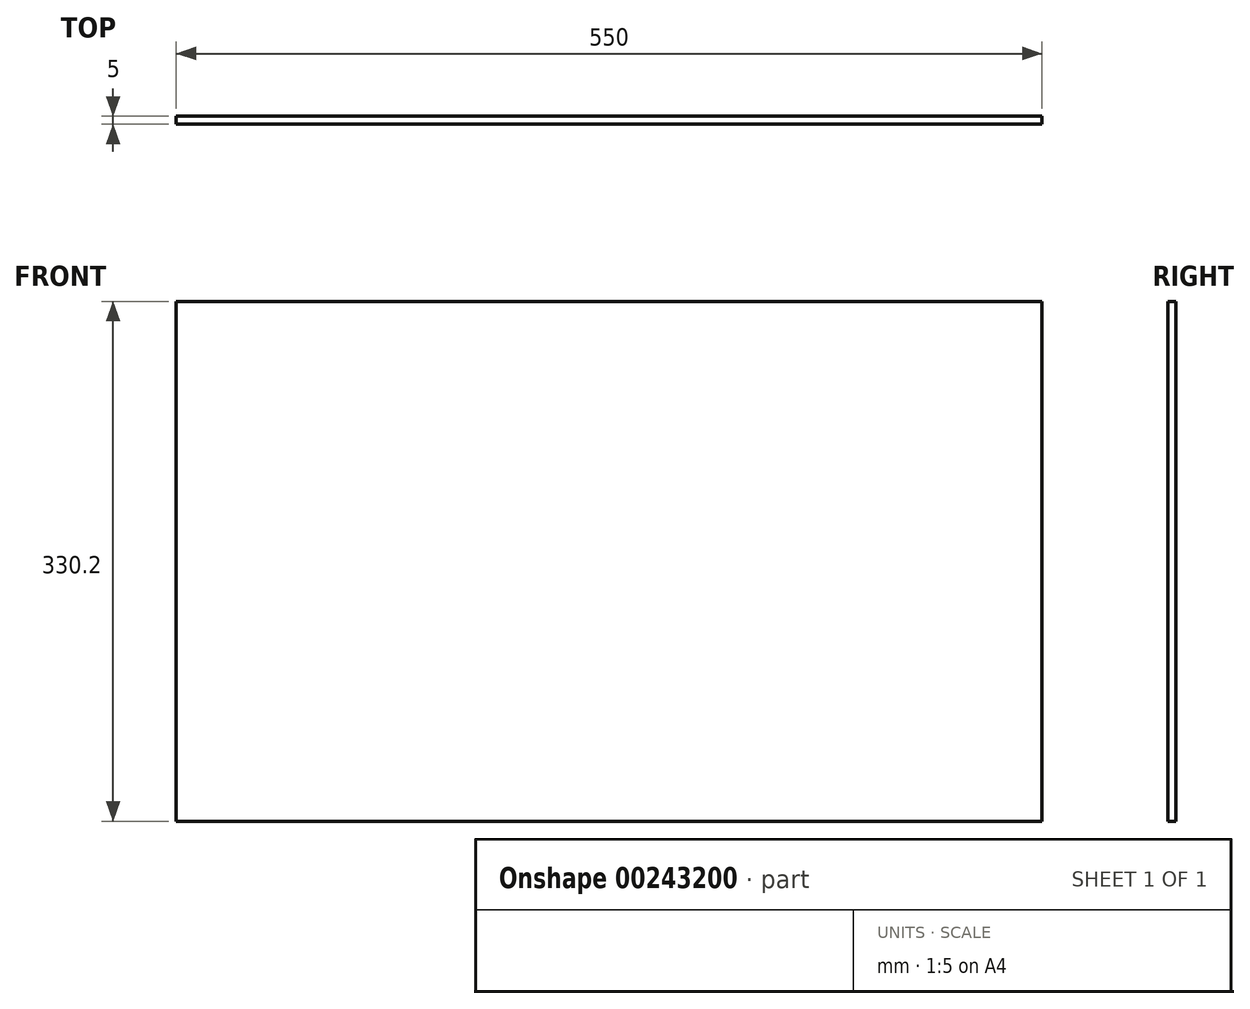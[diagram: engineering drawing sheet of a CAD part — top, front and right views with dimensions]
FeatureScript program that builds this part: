
annotation { "Feature Type Name" : "Feature", "Feature Type Description" : "" }
export const myFeature = defineFeature(function(context is Context, id is Id, definition is map)
    precondition{}
    {
        {
            var Q0;
            Q0=qCreatedBy(makeId("Front.planeOp"),FACE);
            var sketch = newSketch(context, id + "F0", { "sketchPlane" : qUnion([Q0])});
            skLineSegment(sketch, "E0.bottom", {"start": v(-191.75, 43.45) * mm, "end": v(113.25, 43.45) * mm});
            skLineSegment(sketch, "E0.top", {"start": v(-191.75, -73.55) * mm, "end": v(113.25, -73.55) * mm});
            skLineSegment(sketch, "E0.left", {"start": v(-191.75, 43.45) * mm, "end": v(-191.75, -73.55) * mm});
            skLineSegment(sketch, "E0.right", {"start": v(113.25, 43.45) * mm, "end": v(113.25, -73.55) * mm});
            skLineSegment(sketch, "E1.bottom", {"start": v(-203.2, 168.67) * mm, "end": v(0, 168.67) * mm});
            skLineSegment(sketch, "E1.top", {"start": v(-203.2, 98.67) * mm, "end": v(0, 98.67) * mm});
            skLineSegment(sketch, "E1.left", {"start": v(-203.2, 168.67) * mm, "end": v(-203.2, 98.67) * mm});
            skLineSegment(sketch, "E1.right", {"start": v(0, 168.67) * mm, "end": v(0, 98.67) * mm});
            skLineSegment(sketch, "E2.bottom", {"start": v(-191.58, -90.92) * mm, "end": v(11.62, -90.92) * mm});
            skLineSegment(sketch, "E2.top", {"start": v(-191.58, -160.92) * mm, "end": v(11.62, -160.92) * mm});
            skLineSegment(sketch, "E2.left", {"start": v(-191.58, -90.92) * mm, "end": v(-191.58, -160.92) * mm});
            skLineSegment(sketch, "E2.right", {"start": v(11.62, -90.92) * mm, "end": v(11.62, -160.92) * mm});
            skLineSegment(sketch, "E3.bottom", {"start": v(-312.35, 526.53) * mm, "end": v(237.65, 526.53) * mm});
            skLineSegment(sketch, "E3.top", {"start": v(-312.35, 196.33) * mm, "end": v(237.65, 196.33) * mm});
            skLineSegment(sketch, "E3.left", {"start": v(-312.35, 526.53) * mm, "end": v(-312.35, 196.33) * mm});
            skLineSegment(sketch, "E3.right", {"start": v(237.65, 526.53) * mm, "end": v(237.65, 196.33) * mm});
            skLineSegment(sketch, "E4.bottom", {"start": v(32.99, 165.31) * mm, "end": v(56.52, 165.31) * mm});
            skLineSegment(sketch, "E4.top", {"start": v(32.99, 153.55) * mm, "end": v(56.52, 153.55) * mm});
            skLineSegment(sketch, "E4.left", {"start": v(32.99, 165.31) * mm, "end": v(32.99, 153.55) * mm});
            skLineSegment(sketch, "E4.right", {"start": v(56.52, 165.31) * mm, "end": v(56.52, 153.55) * mm});
            skLineSegment(sketch, "E5.bottom", {"start": v(77.44, 163.35) * mm, "end": v(100.98, 163.35) * mm});
            skLineSegment(sketch, "E5.top", {"start": v(77.44, 151.58) * mm, "end": v(100.98, 151.58) * mm});
            skLineSegment(sketch, "E5.left", {"start": v(77.44, 163.35) * mm, "end": v(77.44, 151.58) * mm});
            skLineSegment(sketch, "E5.right", {"start": v(100.98, 163.35) * mm, "end": v(100.98, 151.58) * mm});
            skSolve(sketch);
        }
        {
            var Q0;
            Q0=makeQuery(id+"F0.imprint","IMPRINT",FACE,{"disambiguationData":[TD([[makeQuery(id+"F0.imprint","IMPRINT",EDGE,{"derivedFrom":sQuery(id+"F0.wireOp",EDGE,"E3.bottom")}),-1.0]])]});
            extrude(context, id + "F1", {"entities" : qUnion([Q0]), "depth" : 5 * mm});
        }
    });
